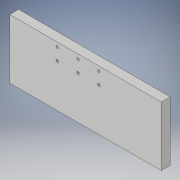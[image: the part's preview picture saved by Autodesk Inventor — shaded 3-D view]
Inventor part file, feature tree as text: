
AUTODESK INVENTOR PART (.ipt)
format: ipt  version: 2018 (Build 220112000, 112)  size: 106,496 bytes
history: native  units: in
note: dims shown in document units (in); Inventor stores cm internally (conversion verified against a paired STEP export)
features: extrude x2, sketch x2
ambient origin geometry x8: Origin, YZ Plane, XZ Plane, XY Plane, X Axis, Y Axis, Z Axis, Center Point
bodies: Solid1 (feature_tree)
feature tree (4):
  extrude  "Extrusion1"  Depth=5.0in
  extrude  "Extrusion2"  Depth=0.75in
  sketch  "Sketch1"  dims[d0=12.75in d1=5.0in]
  sketch  "Sketch2"  dims[d2=0.75in d3=0.0in d4=4.0in d5=0.375in d6=1.75in d7=1.75in d8=1.0in d9=0.21in d10=0.75in d11=0.0in]
